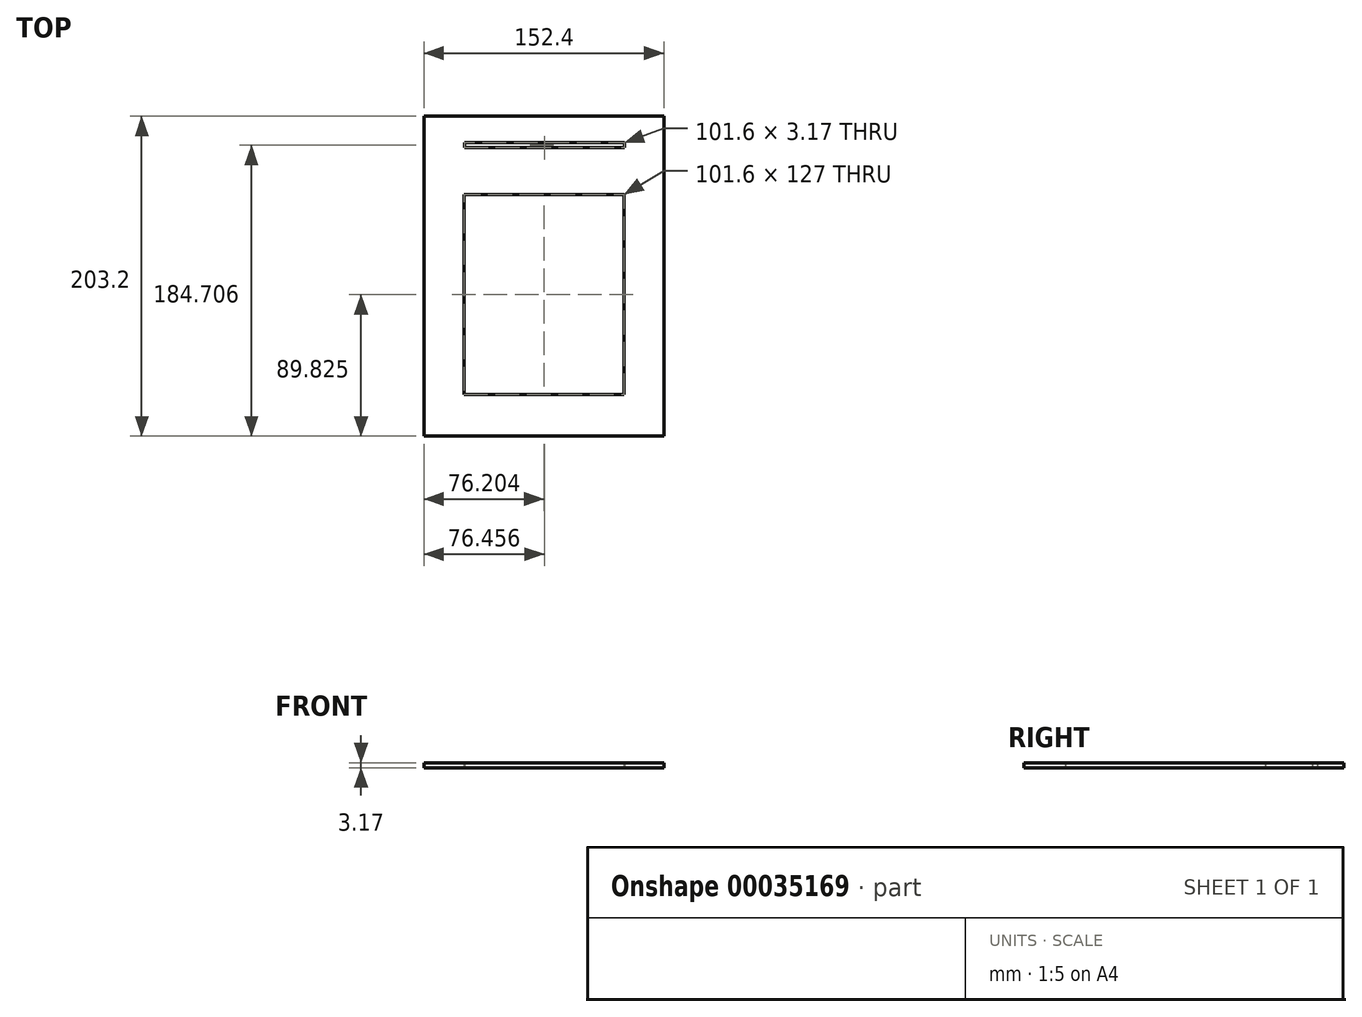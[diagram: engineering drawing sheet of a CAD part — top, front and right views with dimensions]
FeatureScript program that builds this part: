
annotation { "Feature Type Name" : "Feature", "Feature Type Description" : "" }
export const myFeature = defineFeature(function(context is Context, id is Id, definition is map)
    precondition{}
    {
        {
            var Q0;
            Q0=qCreatedBy(makeId("Top.planeOp"),FACE);
            var sketch = newSketch(context, id + "F0", { "sketchPlane" : qUnion([Q0])});
            skLineSegment(sketch, "E0.bottom", {"start": v(-82.49, 98.8) * mm, "end": v(69.91, 98.8) * mm});
            skLineSegment(sketch, "E0.top", {"start": v(-82.49, -104.4) * mm, "end": v(69.91, -104.4) * mm});
            skLineSegment(sketch, "E0.left", {"start": v(-82.49, 98.8) * mm, "end": v(-82.49, -104.4) * mm});
            skLineSegment(sketch, "E0.right", {"start": v(69.91, 98.8) * mm, "end": v(69.91, -104.4) * mm});
            skLineSegment(sketch, "E1.bottom", {"start": v(-56.83, 78.73) * mm, "end": v(44.77, 78.73) * mm});
            skLineSegment(sketch, "E1.top", {"start": v(-56.83, 81.9) * mm, "end": v(44.77, 81.9) * mm});
            skLineSegment(sketch, "E1.left", {"start": v(-56.83, 78.73) * mm, "end": v(-56.83, 81.9) * mm});
            skLineSegment(sketch, "E1.right", {"start": v(44.77, 78.73) * mm, "end": v(44.77, 81.9) * mm});
            skLineSegment(sketch, "E2.bottom", {"start": v(-57.09, 48.94) * mm, "end": v(44.51, 48.94) * mm});
            skLineSegment(sketch, "E2.top", {"start": v(-57.09, -78.06) * mm, "end": v(44.51, -78.06) * mm});
            skLineSegment(sketch, "E2.left", {"start": v(-57.09, 48.94) * mm, "end": v(-57.09, -78.06) * mm});
            skLineSegment(sketch, "E2.right", {"start": v(44.51, 48.94) * mm, "end": v(44.51, -78.06) * mm});
            skSolve(sketch);
        }
        {
            var Q0;
            Q0=makeQuery(id+"F0.imprint","IMPRINT",FACE,{"disambiguationData":[TD([[makeQuery(id+"F0.imprint","IMPRINT",EDGE,{"derivedFrom":sQuery(id+"F0.wireOp",EDGE,"E0.bottom")}),-1.0]])]});
            extrude(context, id + "F1", {"entities" : qUnion([Q0]), "depth" : 3.17 * mm});
        }
    });
